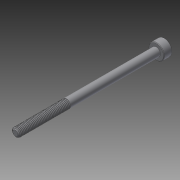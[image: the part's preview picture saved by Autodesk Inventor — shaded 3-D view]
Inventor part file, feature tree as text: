
AUTODESK INVENTOR PART (.ipt)
format: ipt  version: 2015 (Build 190159000, 159)  size: 1,563,648 bytes
history: native  units: in
note: dims shown in document units (in); Inventor stores cm internally (conversion verified against a paired STEP export)
features: revolve x1, other x1, imported_body x1
ambient origin geometry x8: Origin, YZ Plane, XZ Plane, XY Plane, X Axis, Y Axis, Z Axis, Center Point
bodies: Body1 (feature_tree)
feature tree (3):
  revolve  "Revolve1"  [1 undecoded]
  other  "91290A1371"
  imported_body  "Base1"
note: 1 required parameter value undecoded (feature->parameter linkage not recoverable at this tier; creation-order binding heuristic only, values carry confidence <= 0.55)
